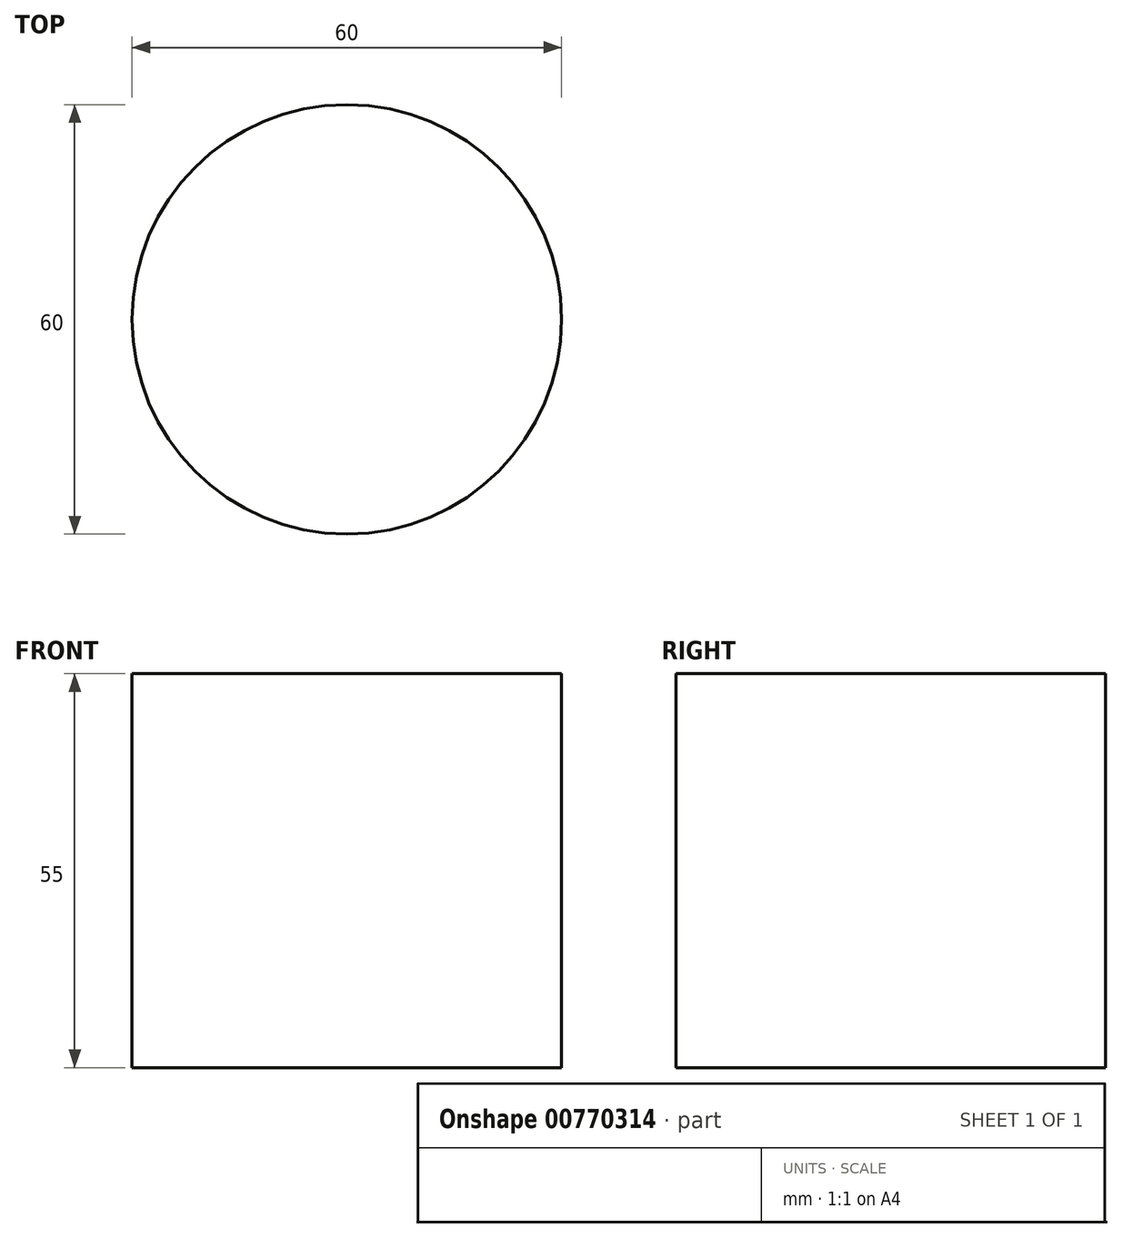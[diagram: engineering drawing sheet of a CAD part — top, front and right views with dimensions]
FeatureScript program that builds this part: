
annotation { "Feature Type Name" : "Feature", "Feature Type Description" : "" }
export const myFeature = defineFeature(function(context is Context, id is Id, definition is map)
    precondition{}
    {
        {
            var Q0;
            Q0=qCreatedBy(makeId("Top.planeOp"),FACE);
            var sketch = newSketch(context, id + "F0", { "sketchPlane" : qUnion([Q0])});
            skCircle(sketch, "E0", {"center": v(0, 0) * mm, "radius": 30 * mm});
            skSolve(sketch);
        }
        {
            var Q0;
            Q0=makeQuery(id+"F0.imprint","IMPRINT",FACE,{"disambiguationData":[TD([[makeQuery(id+"F0.imprint","IMPRINT",EDGE,{"derivedFrom":sQuery(id+"F0.wireOp",EDGE,"E0")}),1.0]])]});
            extrude(context, id + "F1", {"entities" : qUnion([Q0]), "depth" : 55 * mm, "offsetDistance" : 25 * mm});
        }
    });
